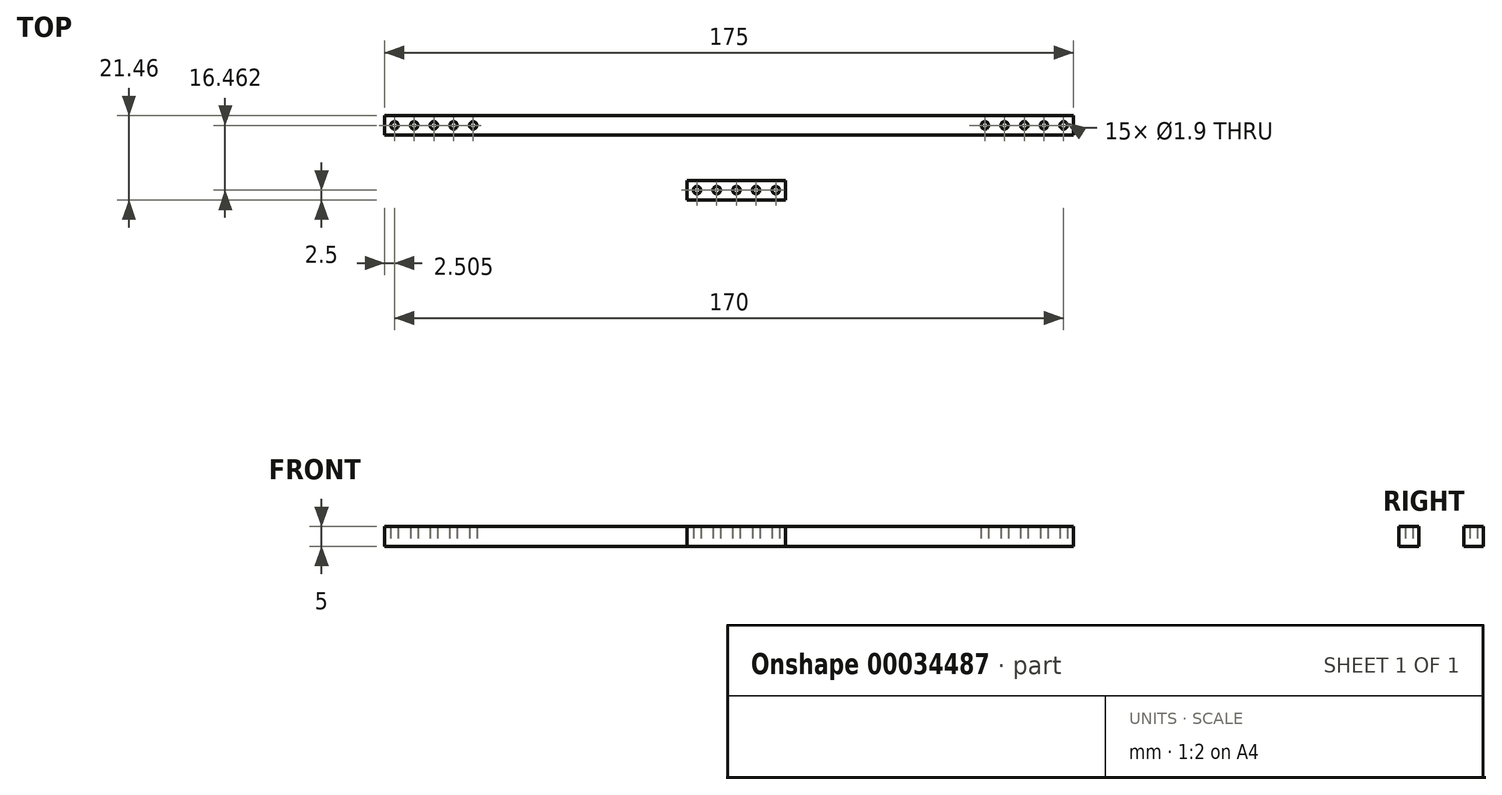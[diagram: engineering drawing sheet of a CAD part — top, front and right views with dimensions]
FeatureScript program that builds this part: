
annotation { "Feature Type Name" : "Feature", "Feature Type Description" : "" }
export const myFeature = defineFeature(function(context is Context, id is Id, definition is map)
    precondition{}
    {
        {
            var Q0;
            Q0=qCreatedBy(makeId("Top.planeOp"),FACE);
            var sketch = newSketch(context, id + "F0", { "sketchPlane" : qUnion([Q0])});
            skLineSegment(sketch, "E0", {"start": v(-8.28, -8.26) * mm, "end": v(11.72, -8.26) * mm, "construction": true});
            skCircle(sketch, "E1", {"center": v(-8.28, -8.26) * mm, "radius": 0.95 * mm});
            skCircle(sketch, "E2", {"center": v(11.72, -8.26) * mm, "radius": 0.95 * mm});
            skLineSegment(sketch, "E3", {"start": v(-8.28, -8.26) * mm, "end": v(-10.78, -8.26) * mm, "construction": true});
            skLineSegment(sketch, "E4", {"start": v(11.72, -8.26) * mm, "end": v(14.22, -8.26) * mm, "construction": true});
            skLineSegment(sketch, "E5", {"start": v(-10.78, -8.26) * mm, "end": v(-10.78, -5.76) * mm, "construction": true});
            skLineSegment(sketch, "E6", {"start": v(14.22, -8.26) * mm, "end": v(14.22, -10.76) * mm, "construction": true});
            skLineSegment(sketch, "E7.bottom", {"start": v(-10.78, -5.76) * mm, "end": v(14.22, -5.76) * mm});
            skLineSegment(sketch, "E7.top", {"start": v(-10.78, -10.76) * mm, "end": v(14.22, -10.76) * mm});
            skLineSegment(sketch, "E7.left", {"start": v(-10.78, -5.76) * mm, "end": v(-10.78, -10.76) * mm});
            skLineSegment(sketch, "E7.right", {"start": v(14.22, -5.76) * mm, "end": v(14.22, -10.76) * mm});
            skCircle(sketch, "E8.1.0.0", {"center": v(-3.28, -8.26) * mm, "radius": 0.95 * mm});
            skCircle(sketch, "E8.2.0.0", {"center": v(1.72, -8.26) * mm, "radius": 0.95 * mm});
            skCircle(sketch, "E8.3.0.0", {"center": v(6.72, -8.26) * mm, "radius": 0.95 * mm});
            skLineSegment(sketch, "E8.direction1", {"start": v(-8.28, -8.26) * mm, "end": v(-3.28, -8.26) * mm, "construction": true});
            skLineSegment(sketch, "E9", {"start": v(-85.15, 8.2) * mm, "end": v(84.85, 8.2) * mm, "construction": true});
            skLineSegment(sketch, "E10.bottom", {"start": v(-87.65, 10.7) * mm, "end": v(87.35, 10.7) * mm});
            skLineSegment(sketch, "E10.top", {"start": v(-87.65, 5.7) * mm, "end": v(87.35, 5.7) * mm});
            skCircle(sketch, "E11.4.0.0", {"center": v(64.85, 8.2) * mm, "radius": 0.95 * mm});
            skCircle(sketch, "E11.2.0.0", {"center": v(74.85, 8.2) * mm, "radius": 0.95 * mm});
            skCircle(sketch, "E12.3.0.0", {"center": v(-70.15, 8.2) * mm, "radius": 0.95 * mm});
            skCircle(sketch, "E12.4.0.0", {"center": v(-65.15, 8.2) * mm, "radius": 0.95 * mm});
            skCircle(sketch, "E12.2.0.0", {"center": v(-75.15, 8.2) * mm, "radius": 0.95 * mm});
            skCircle(sketch, "E11.3.0.0", {"center": v(69.85, 8.2) * mm, "radius": 0.95 * mm});
            skLineSegment(sketch, "E12.direction1", {"start": v(-85.15, 8.2) * mm, "end": v(-80.15, 8.2) * mm, "construction": true});
            skCircle(sketch, "E12.1.0.0", {"center": v(-80.15, 8.2) * mm, "radius": 0.95 * mm});
            skLineSegment(sketch, "E11.direction1", {"start": v(84.85, 8.2) * mm, "end": v(79.85, 8.2) * mm, "construction": true});
            skCircle(sketch, "E11.1.0.0", {"center": v(79.85, 8.2) * mm, "radius": 0.95 * mm});
            skLineSegment(sketch, "E10.left", {"start": v(-87.65, 10.7) * mm, "end": v(-87.65, 5.7) * mm});
            skLineSegment(sketch, "E10.right", {"start": v(87.35, 10.7) * mm, "end": v(87.35, 5.7) * mm});
            skCircle(sketch, "E13", {"center": v(-85.15, 8.2) * mm, "radius": 0.95 * mm});
            skCircle(sketch, "E14", {"center": v(84.85, 8.2) * mm, "radius": 0.95 * mm});
            skLineSegment(sketch, "E15", {"start": v(-85.15, 8.2) * mm, "end": v(-87.65, 8.2) * mm, "construction": true});
            skLineSegment(sketch, "E16", {"start": v(84.85, 8.2) * mm, "end": v(87.35, 8.2) * mm, "construction": true});
            skLineSegment(sketch, "E17", {"start": v(-87.65, 8.2) * mm, "end": v(-87.65, 10.7) * mm, "construction": true});
            skLineSegment(sketch, "E18", {"start": v(87.35, 8.2) * mm, "end": v(87.35, 5.7) * mm, "construction": true});
            skSolve(sketch);
        }
        {
            var Q0;
            Q0 = qSketchRegion(id + "F0", true);
            extrude(context, id + "F1", {"entities" : qUnion([Q0]), "depth" : 5 * mm});
        }
    });
